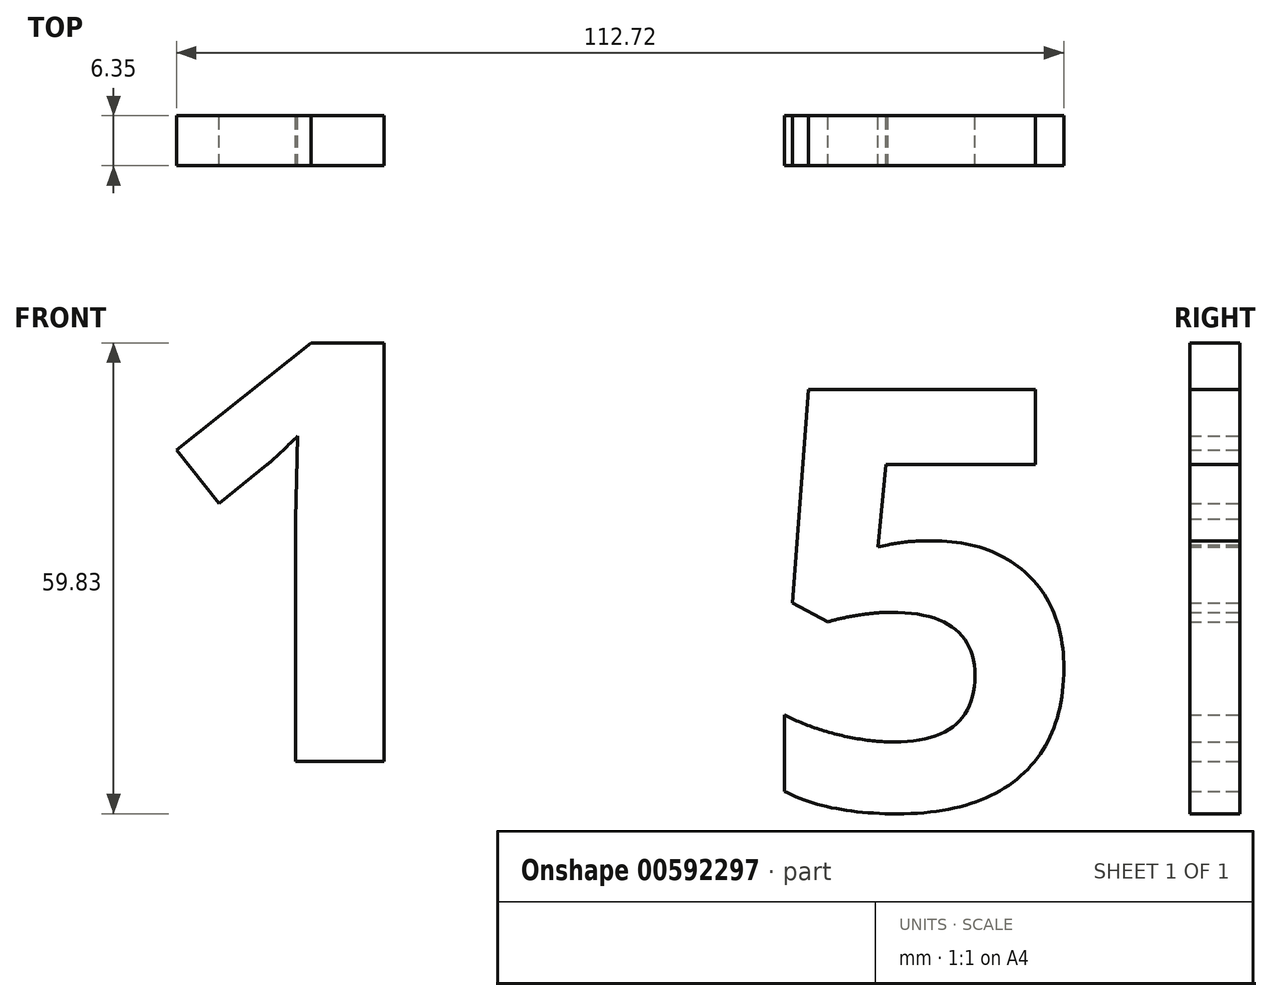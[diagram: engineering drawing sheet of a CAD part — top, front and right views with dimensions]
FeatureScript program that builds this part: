
annotation { "Feature Type Name" : "Feature", "Feature Type Description" : "" }
export const myFeature = defineFeature(function(context is Context, id is Id, definition is map)
    precondition{}
    {
        {
            var Q0;
            Q0=qCreatedBy(makeId("Front.planeOp"),FACE);
            var sketch = newSketch(context, id + "F0", { "sketchPlane" : qUnion([Q0])});
            skText(sketch, "E0", { "text": "1", "fontName": "OpenSans-Bold.ttf"});
            const initialGuessF0  = {"E0": [-0.10027, -0.01628, 1, 0, 0.0536]};
            skSetInitialGuess(sketch, initialGuessF0);
            skSolve(sketch);
        }
        {
            var Q0;
            Q0=makeQuery(id+"F0.imprint","IMPRINT",FACE,{"disambiguationData":[TD([[makeQuery(id+"F0.imprint","IMPRINT",EDGE,{"derivedFrom":sQuery(id+"F0.wireOp",EDGE,"E0.sketch_text.stroke-0")}),-1.0]])]});
            extrude(context, id + "F1", {"entities" : qUnion([Q0]), "depth" : 6.35 * mm, "offsetDistance" : 25.4 * mm});
        }
        {
            var Q0;
            Q0=qCreatedBy(makeId("Front.planeOp"),FACE);
            var sketch = newSketch(context, id + "F2", { "sketchPlane" : qUnion([Q0])});
            skText(sketch, "E1", { "text": "5", "fontName": "OpenSans-Bold.ttf"});
            const initialGuessF2  = {"E1": [-0.0223, -0.02223, 1, 0, 0.0536]};
            skSetInitialGuess(sketch, initialGuessF2);
            skSolve(sketch);
        }
        {
            var Q0;
            Q0=makeQuery(id+"F2.imprint","IMPRINT",FACE,{"disambiguationData":[TD([[makeQuery(id+"F2.imprint","IMPRINT",EDGE,{"derivedFrom":sQuery(id+"F2.wireOp",EDGE,"E1.sketch_text.stroke-0")}),-1.0]])]});
            extrude(context, id + "F3", {"entities" : qUnion([Q0]), "depth" : 6.35 * mm, "offsetDistance" : 25.4 * mm});
        }
    });
